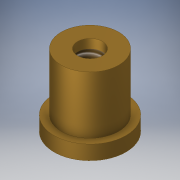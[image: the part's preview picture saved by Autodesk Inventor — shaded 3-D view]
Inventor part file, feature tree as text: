
AUTODESK INVENTOR PART (.ipt)
format: ipt  version: 2018 (Build 220112000, 112)  size: 115,712 bytes
history: native  units: in
note: dims shown in document units (in); Inventor stores cm internally (conversion verified against a paired STEP export)
features: sketch x3, extrude x2, hole x1
ambient origin geometry x8: Origin, YZ Plane, XZ Plane, XY Plane, X Axis, Y Axis, Z Axis, Center Point
bodies: Solid1 (feature_tree)
feature tree (6):
  extrude  "Extrusion1"  Depth=0.375in TaperAngle=0.0deg
  extrude  "Extrusion2"  Depth=0.3in
  hole  "Hole1"  [1 undecoded]
  sketch  "Sketch1"  dims[d0=0.375in d1=0.375in d2=0.0in]
  sketch  "Sketch2"  dims[d3=0.5in d4=0.3in]
  sketch  "Sketch3"  dims[d5=0.3in d6=0.0in d7=0.13in d8=0.328in d9=0.375in d10=0.25in d11=0.5635in d12=0.484in d13=0.8108in]
note: 1 required parameter value undecoded (feature->parameter linkage not recoverable at this tier; creation-order binding heuristic only, values carry confidence <= 0.55)
